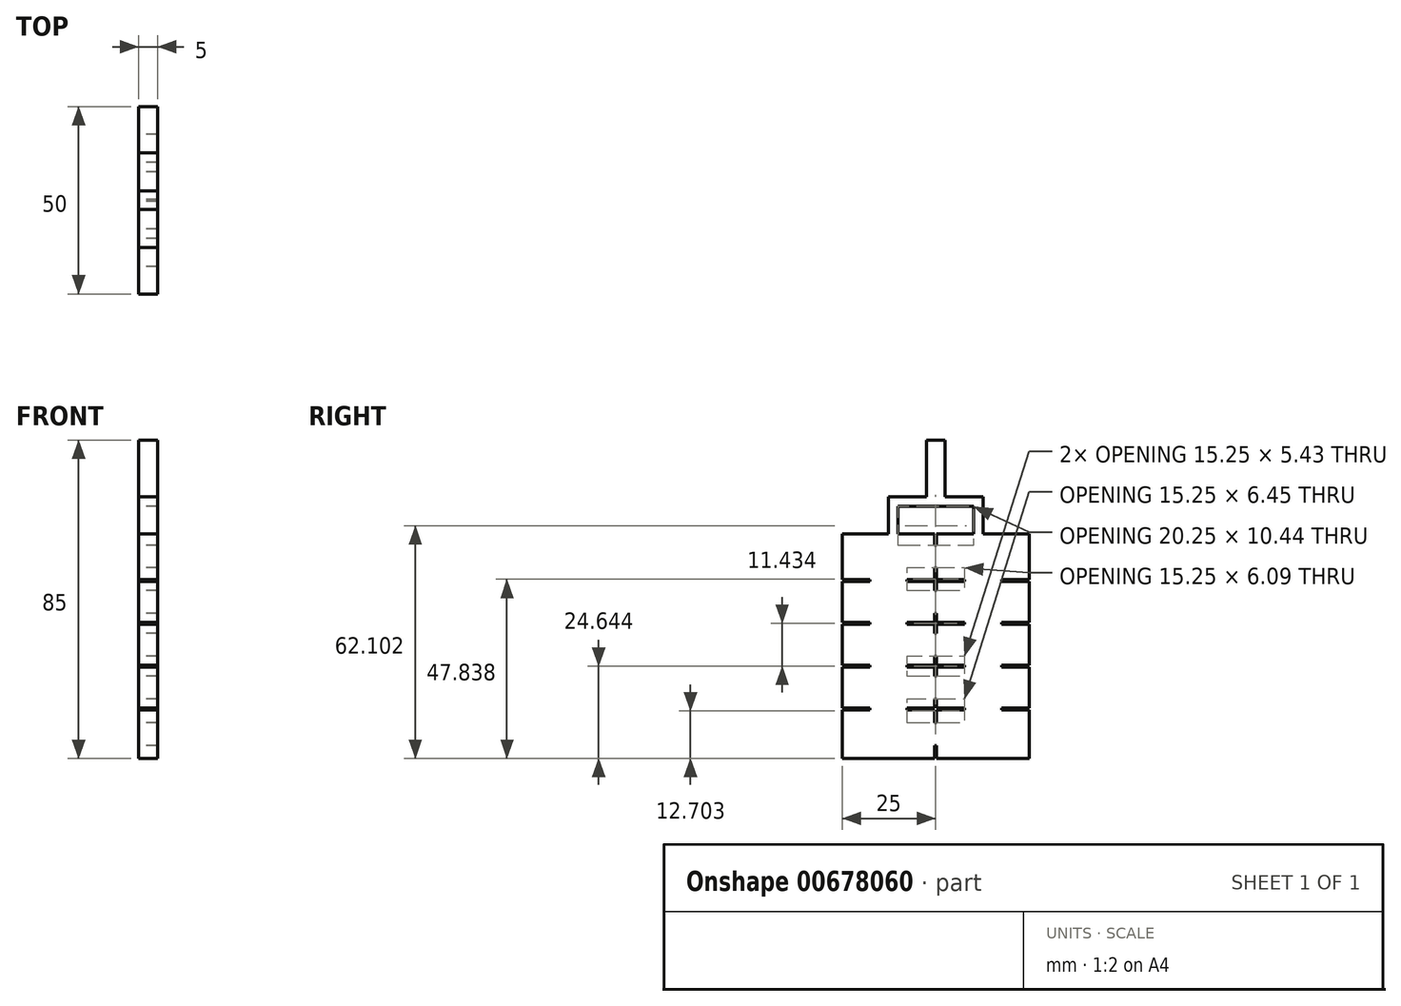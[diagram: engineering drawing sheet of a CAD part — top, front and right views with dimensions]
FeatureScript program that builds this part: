
annotation { "Feature Type Name" : "Feature", "Feature Type Description" : "" }
export const myFeature = defineFeature(function(context is Context, id is Id, definition is map)
    precondition{}
    {
        {
            var Q0;
            Q0=qCreatedBy(makeId("Right.planeOp"),FACE);
            var sketch = newSketch(context, id + "F0", { "sketchPlane" : qUnion([Q0])});
            skPoint(sketch, "E0.0", {"position": v(0, 0) * mm});
            skLineSegment(sketch, "E1.bottom", {"start": v(0, 0) * mm, "end": v(12.38, 0) * mm});
            skLineSegment(sketch, "E1.top", {"start": v(0, -60) * mm, "end": v(24.75, -60) * mm});
            skLineSegment(sketch, "E1.left", {"start": v(0, 0) * mm, "end": v(0, -12.24) * mm});
            skLineSegment(sketch, "E1.right", {"start": v(50, 0) * mm, "end": v(50, -12.24) * mm});
            skPoint(sketch, "E2.MirrorP", {"position": v(11.5, 0) * mm});
            skPoint(sketch, "E3.MirrorP", {"position": v(11.5, -2) * mm});
            skPoint(sketch, "E4.MirrorP", {"position": v(18.5, 0) * mm});
            skPoint(sketch, "E5.MirrorP", {"position": v(30, 0) * mm});
            skLineSegment(sketch, "E6.0", {"start": v(25.25, -60) * mm, "end": v(25.25, -56.52) * mm});
            skLineSegment(sketch, "E7.0", {"start": v(0, -12.24) * mm, "end": v(7.38, -12.24) * mm});
            skLineSegment(sketch, "E8.0", {"start": v(0, -12.74) * mm, "end": v(7.38, -12.74) * mm});
            skLineSegment(sketch, "E9.trimOffspring", {"start": v(25.25, -3.12) * mm, "end": v(25.25, -1.3) * mm});
            skLineSegment(sketch, "E10.trimOffspring", {"start": v(25.25, -12.24) * mm, "end": v(32.63, -12.24) * mm});
            skLineSegment(sketch, "E11.trimOffspring", {"start": v(25.25, -12.24) * mm, "end": v(25.25, -9.12) * mm});
            skLineSegment(sketch, "E12.trimOffspring", {"start": v(25.25, -12.74) * mm, "end": v(32.63, -12.74) * mm});
            skLineSegment(sketch, "E13.trimOffspring", {"start": v(25.25, -15.2) * mm, "end": v(25.25, -12.74) * mm});
            skLineSegment(sketch, "E14.0", {"start": v(0, -23.67) * mm, "end": v(7.38, -23.67) * mm});
            skLineSegment(sketch, "E15.0", {"start": v(0, -24.17) * mm, "end": v(7.38, -24.17) * mm});
            skLineSegment(sketch, "E16.trimOffspring", {"start": v(25.25, -23.67) * mm, "end": v(32.63, -23.67) * mm});
            skLineSegment(sketch, "E17.trimOffspring", {"start": v(25.25, -23.67) * mm, "end": v(25.25, -21.2) * mm});
            skLineSegment(sketch, "E18.trimOffspring", {"start": v(25.25, -24.17) * mm, "end": v(32.63, -24.17) * mm});
            skLineSegment(sketch, "E19.trimOffspring", {"start": v(25.25, -26.64) * mm, "end": v(25.25, -24.17) * mm});
            skLineSegment(sketch, "E20.trimOffspring", {"start": v(24.75, -26.64) * mm, "end": v(24.75, -24.17) * mm});
            skLineSegment(sketch, "E21.0", {"start": v(0, -35.1) * mm, "end": v(7.38, -35.1) * mm});
            skLineSegment(sketch, "E22.0", {"start": v(0, -35.6) * mm, "end": v(7.38, -35.6) * mm});
            skLineSegment(sketch, "E23.trimOffspring", {"start": v(25.25, -35.1) * mm, "end": v(32.63, -35.1) * mm});
            skLineSegment(sketch, "E24.trimOffspring", {"start": v(25.25, -35.1) * mm, "end": v(25.25, -32.64) * mm});
            skLineSegment(sketch, "E25.trimOffspring", {"start": v(24.75, -35.1) * mm, "end": v(24.75, -32.64) * mm});
            skLineSegment(sketch, "E26.trimOffspring", {"start": v(25.25, -35.6) * mm, "end": v(32.63, -35.6) * mm});
            skLineSegment(sketch, "E27.trimOffspring", {"start": v(25.25, -38.07) * mm, "end": v(25.25, -35.6) * mm});
            skLineSegment(sketch, "E28.trimOffspring", {"start": v(24.75, -38.07) * mm, "end": v(24.75, -35.6) * mm});
            skLineSegment(sketch, "E29.0", {"start": v(0, -46.54) * mm, "end": v(7.38, -46.54) * mm});
            skLineSegment(sketch, "E30.0", {"start": v(0, -47.04) * mm, "end": v(7.38, -47.04) * mm});
            skLineSegment(sketch, "E31.trimOffspring", {"start": v(25.25, -46.54) * mm, "end": v(32.63, -46.54) * mm});
            skLineSegment(sketch, "E32.trimOffspring", {"start": v(25.25, -46.54) * mm, "end": v(25.25, -44.07) * mm});
            skLineSegment(sketch, "E33.trimOffspring", {"start": v(24.75, -46.54) * mm, "end": v(24.75, -44.07) * mm});
            skLineSegment(sketch, "E34.trimOffspring", {"start": v(25.25, -47.04) * mm, "end": v(32.63, -47.04) * mm});
            skLineSegment(sketch, "E35.trimOffspring", {"start": v(25.25, -50.52) * mm, "end": v(25.25, -47.04) * mm});
            skLineSegment(sketch, "E36.trimOffspring", {"start": v(0, -12.74) * mm, "end": v(0, -23.67) * mm});
            skLineSegment(sketch, "E37.trimOffspring", {"start": v(0, -24.17) * mm, "end": v(0, -35.1) * mm});
            skLineSegment(sketch, "E38.trimOffspring", {"start": v(0, -35.6) * mm, "end": v(0, -46.54) * mm});
            skLineSegment(sketch, "E39.trimOffspring", {"start": v(0, -47.04) * mm, "end": v(0, -60) * mm});
            skLineSegment(sketch, "E40.trimOffspring", {"start": v(50, -47.04) * mm, "end": v(50, -60) * mm});
            skLineSegment(sketch, "E41.trimOffspring", {"start": v(50, -35.6) * mm, "end": v(50, -46.54) * mm});
            skLineSegment(sketch, "E42.trimOffspring", {"start": v(50, -12.74) * mm, "end": v(50, -23.67) * mm});
            skLineSegment(sketch, "E43.trimOffspring", {"start": v(50, -24.17) * mm, "end": v(50, -35.1) * mm});
            skLineSegment(sketch, "E44.0", {"start": v(17.38, -12.74) * mm, "end": v(17.38, -12.24) * mm});
            skLineSegment(sketch, "E45.0", {"start": v(7.38, -12.74) * mm, "end": v(7.38, -12.24) * mm});
            skLineSegment(sketch, "E46", {"start": v(24.75, -12.24) * mm, "end": v(24.75, -9.12) * mm});
            skLineSegment(sketch, "E47.0", {"start": v(24.75, -9.12) * mm, "end": v(25.25, -9.12) * mm});
            skLineSegment(sketch, "E48.0", {"start": v(24.75, -3.12) * mm, "end": v(25.25, -3.12) * mm});
            skLineSegment(sketch, "E49", {"start": v(24.75, -12.74) * mm, "end": v(24.75, -15.2) * mm});
            skLineSegment(sketch, "E50.0", {"start": v(24.75, -21.2) * mm, "end": v(25.25, -21.2) * mm});
            skLineSegment(sketch, "E51.0", {"start": v(24.75, -15.2) * mm, "end": v(25.25, -15.2) * mm});
            skLineSegment(sketch, "E52", {"start": v(25.25, -1.3) * mm, "end": v(25.25, 0) * mm});
            skLineSegment(sketch, "E53.trimOffspring", {"start": v(25.25, 0) * mm, "end": v(35.12, 0) * mm});
            skPoint(sketch, "E54.start.orphan", {"position": v(24.75, -6.12) * mm});
            skLineSegment(sketch, "E55", {"start": v(7.38, -12.24) * mm, "end": v(7.38, -12.74) * mm});
            skLineSegment(sketch, "E56", {"start": v(17.38, -12.24) * mm, "end": v(17.38, -12.74) * mm});
            skLineSegment(sketch, "E57.trimOffspring", {"start": v(7.38, -23.67) * mm, "end": v(7.38, -24.17) * mm});
            skLineSegment(sketch, "E58.trimOffspring", {"start": v(17.38, -23.67) * mm, "end": v(17.38, -24.17) * mm});
            skLineSegment(sketch, "E59.trimOffspring", {"start": v(7.38, -35.1) * mm, "end": v(7.38, -35.6) * mm});
            skLineSegment(sketch, "E60.trimOffspring", {"start": v(17.38, -35.1) * mm, "end": v(17.38, -35.6) * mm});
            skLineSegment(sketch, "E61.trimOffspring", {"start": v(7.38, -46.54) * mm, "end": v(7.38, -47.04) * mm});
            skLineSegment(sketch, "E62.trimOffspring", {"start": v(17.38, -46.54) * mm, "end": v(17.38, -47.04) * mm});
            skLineSegment(sketch, "E63.trimOffspring", {"start": v(17.38, -46.54) * mm, "end": v(24.75, -46.54) * mm});
            skLineSegment(sketch, "E64.trimOffspring", {"start": v(17.38, -47.04) * mm, "end": v(24.75, -47.04) * mm});
            skLineSegment(sketch, "E65.trimOffspring", {"start": v(17.38, -35.1) * mm, "end": v(24.75, -35.1) * mm});
            skLineSegment(sketch, "E66.trimOffspring", {"start": v(17.38, -35.6) * mm, "end": v(24.75, -35.6) * mm});
            skLineSegment(sketch, "E67.trimOffspring", {"start": v(17.37, -23.67) * mm, "end": v(24.75, -23.67) * mm});
            skLineSegment(sketch, "E68.trimOffspring", {"start": v(17.37, -24.17) * mm, "end": v(24.75, -24.17) * mm});
            skLineSegment(sketch, "E69.trimOffspring", {"start": v(17.38, -12.24) * mm, "end": v(24.75, -12.24) * mm});
            skPoint(sketch, "E70.start.orphan", {"position": v(12.38, -12.74) * mm});
            skPoint(sketch, "E71.orphan", {"position": v(12.38, -12.24) * mm});
            skLineSegment(sketch, "E72.trimOffspring", {"start": v(17.38, -12.74) * mm, "end": v(24.75, -12.74) * mm});
            skLineSegment(sketch, "E73.0", {"start": v(32.63, -12.24) * mm, "end": v(32.63, -12.74) * mm});
            skLineSegment(sketch, "E74.0", {"start": v(42.62, -12.24) * mm, "end": v(42.62, -12.74) * mm});
            skLineSegment(sketch, "E75.trimOffspring", {"start": v(32.63, -23.67) * mm, "end": v(32.63, -24.17) * mm});
            skLineSegment(sketch, "E76.trimOffspring", {"start": v(42.62, -23.67) * mm, "end": v(42.62, -24.17) * mm});
            skLineSegment(sketch, "E77.trimOffspring", {"start": v(32.63, -35.1) * mm, "end": v(32.63, -35.6) * mm});
            skLineSegment(sketch, "E78.trimOffspring", {"start": v(42.62, -35.1) * mm, "end": v(42.62, -35.6) * mm});
            skLineSegment(sketch, "E79.trimOffspring", {"start": v(32.63, -46.54) * mm, "end": v(32.63, -47.04) * mm});
            skLineSegment(sketch, "E80.trimOffspring", {"start": v(42.62, -46.54) * mm, "end": v(42.62, -47.04) * mm});
            skLineSegment(sketch, "E81.0", {"start": v(24.75, -26.64) * mm, "end": v(25.25, -26.64) * mm});
            skLineSegment(sketch, "E82.0", {"start": v(24.75, -32.64) * mm, "end": v(25.25, -32.64) * mm});
            skLineSegment(sketch, "E83.0", {"start": v(24.75, -38.07) * mm, "end": v(25.25, -38.07) * mm});
            skLineSegment(sketch, "E84.0", {"start": v(24.75, -44.07) * mm, "end": v(25.25, -44.07) * mm});
            skLineSegment(sketch, "E85", {"start": v(24.75, -47.04) * mm, "end": v(24.75, -50.52) * mm});
            skLineSegment(sketch, "E86.0", {"start": v(24.75, -56.52) * mm, "end": v(25.25, -56.52) * mm});
            skLineSegment(sketch, "E87.0", {"start": v(24.75, -50.52) * mm, "end": v(25.25, -50.52) * mm});
            skLineSegment(sketch, "E88.trimOffspring", {"start": v(24.75, -56.52) * mm, "end": v(24.75, -60) * mm});
            skLineSegment(sketch, "E89.trimOffspring", {"start": v(25.25, -60) * mm, "end": v(50, -60) * mm});
            skLineSegment(sketch, "E90.trimOffspring", {"start": v(42.62, -46.54) * mm, "end": v(50, -46.54) * mm});
            skLineSegment(sketch, "E91.trimOffspring", {"start": v(42.62, -47.04) * mm, "end": v(50, -47.04) * mm});
            skLineSegment(sketch, "E92.trimOffspring", {"start": v(42.62, -35.1) * mm, "end": v(50, -35.1) * mm});
            skLineSegment(sketch, "E93.trimOffspring", {"start": v(42.62, -35.6) * mm, "end": v(50, -35.6) * mm});
            skLineSegment(sketch, "E94.trimOffspring", {"start": v(42.62, -23.67) * mm, "end": v(50, -23.67) * mm});
            skLineSegment(sketch, "E95.trimOffspring", {"start": v(42.62, -24.17) * mm, "end": v(50, -24.17) * mm});
            skLineSegment(sketch, "E96.trimOffspring", {"start": v(42.62, -12.24) * mm, "end": v(50, -12.24) * mm});
            skLineSegment(sketch, "E97.trimOffspring", {"start": v(42.62, -12.74) * mm, "end": v(50, -12.74) * mm});
            skLineSegment(sketch, "E98.trimOffspring", {"start": v(24.75, -21.2) * mm, "end": v(24.75, -23.67) * mm});
            skPoint(sketch, "E99.end.orphan", {"position": v(25.25, -18.2) * mm});
            skPoint(sketch, "E99.start.orphan", {"position": v(24.75, -18.2) * mm});
            skPoint(sketch, "E100.orphan", {"position": v(25.25, -17.95) * mm});
            skPoint(sketch, "E101.end.orphan", {"position": v(25.25, -18.45) * mm});
            skLineSegment(sketch, "E102.trimOffspring", {"start": v(24.75, -3.12) * mm, "end": v(24.75, 0) * mm});
            skLineSegment(sketch, "E103", {"start": v(12.38, 0) * mm, "end": v(12.38, 9.82) * mm});
            skLineSegment(sketch, "E104.0", {"start": v(14.88, 0) * mm, "end": v(14.88, 7.32) * mm});
            skLineSegment(sketch, "E105", {"start": v(37.63, 0) * mm, "end": v(37.63, 9.82) * mm});
            skLineSegment(sketch, "E106.0", {"start": v(35.12, 0) * mm, "end": v(35.12, 7.32) * mm});
            skLineSegment(sketch, "E107", {"start": v(12.38, 9.82) * mm, "end": v(22.5, 9.82) * mm});
            skLineSegment(sketch, "E108.0", {"start": v(14.88, 7.32) * mm, "end": v(35.12, 7.32) * mm});
            skLineSegment(sketch, "E109.0", {"start": v(27.5, 9.82) * mm, "end": v(27.5, 25) * mm});
            skLineSegment(sketch, "E110.0", {"start": v(22.5, 9.82) * mm, "end": v(22.5, 25) * mm});
            skPoint(sketch, "E111.orphan", {"position": v(14.88, 25) * mm});
            skPoint(sketch, "E112.orphan", {"position": v(37.63, 25) * mm});
            skLineSegment(sketch, "E113", {"start": v(22.5, 25) * mm, "end": v(27.5, 25) * mm});
            skLineSegment(sketch, "E114.trimOffspring", {"start": v(14.88, 0) * mm, "end": v(24.75, 0) * mm});
            skLineSegment(sketch, "E115.trimOffspring", {"start": v(37.63, 0) * mm, "end": v(50, 0) * mm});
            skLineSegment(sketch, "E116.trimOffspring", {"start": v(27.5, 9.82) * mm, "end": v(37.63, 9.82) * mm});
            skSolve(sketch);
        }
        {
            var Q0;
            {var subQ1=sQuery(id+"F0.wireOp",EDGE,"6f222dcf-cafe-427f-96f1-de862232ba62.0");Q0=makeQuery(id+"F0.imprint","IMPRINT",FACE,{"disambiguationData":[TD([[makeQuery(id+"F0.imprint","IMPRINT",EDGE,{"derivedFrom":subQ1}),-1.0]])]});}
            var Q1;
            {var subQ1=sQuery(id+"F0.wireOp",EDGE,"9ddca581-0f96-48d2-9b8e-d0e5be099db1.trimOffspring");Q1=makeQuery(id+"F0.imprint","IMPRINT",FACE,{"disambiguationData":[TD([[makeQuery(id+"F0.imprint","IMPRINT",EDGE,{"derivedFrom":subQ1}),-1.0]])]});}
            var Q2;
            Q2=makeQuery(id+"F0.imprint","IMPRINT",FACE,{"disambiguationData":[TD([[makeQuery(id+"F0.imprint","IMPRINT",EDGE,{"derivedFrom":sQuery(id+"F0.wireOp",EDGE,"E8.0")}),-1.0]])]});
            var Q3;
            Q3=makeQuery(id+"F0.imprint","IMPRINT",FACE,{"disambiguationData":[TD([[makeQuery(id+"F0.imprint","IMPRINT",EDGE,{"derivedFrom":sQuery(id+"F0.wireOp",EDGE,"E12.trimOffspring")}),-1.0]])]});
            var Q4;
            Q4=makeQuery(id+"F0.imprint","IMPRINT",FACE,{"disambiguationData":[TD([[makeQuery(id+"F0.imprint","IMPRINT",EDGE,{"derivedFrom":sQuery(id+"F0.wireOp",EDGE,"E18.trimOffspring")}),-1.0]])]});
            var Q5;
            Q5=makeQuery(id+"F0.imprint","IMPRINT",FACE,{"disambiguationData":[TD([[makeQuery(id+"F0.imprint","IMPRINT",EDGE,{"derivedFrom":sQuery(id+"F0.wireOp",EDGE,"E15.0")}),-1.0]])]});
            var Q6;
            Q6=makeQuery(id+"F0.imprint","IMPRINT",FACE,{"disambiguationData":[TD([[makeQuery(id+"F0.imprint","IMPRINT",EDGE,{"derivedFrom":sQuery(id+"F0.wireOp",EDGE,"E22.0")}),-1.0]])]});
            var Q7;
            Q7=makeQuery(id+"F0.imprint","IMPRINT",FACE,{"disambiguationData":[TD([[makeQuery(id+"F0.imprint","IMPRINT",EDGE,{"derivedFrom":sQuery(id+"F0.wireOp",EDGE,"E26.trimOffspring")}),-1.0]])]});
            var Q8;
            {var subQ0=sQuery(id+"F0.wireOp",EDGE,"E6.0");Q8=makeQuery(id+"F0.imprint","IMPRINT",FACE,{"disambiguationData":[TD([[makeQuery(id+"F0.imprint","IMPRINT",EDGE,{"derivedFrom":subQ0}),-1.0]])]});}
            var Q9;
            {var subQ0=sQuery(id+"F0.wireOp",EDGE,"52d86100-12cc-4532-affd-39e9c9b04a49.0");Q9=makeQuery(id+"F0.imprint","IMPRINT",FACE,{"disambiguationData":[TD([[makeQuery(id+"F0.imprint","IMPRINT",EDGE,{"derivedFrom":subQ0}),1.0]])]});}
            extrude(context, id + "F1", {"entities" : qUnion([Q0, Q1, Q2, Q3, Q4, Q5, Q6, Q7, Q8, Q9]), "depth" : 5 * mm, "offsetDistance" : 25 * mm});
        }
    });
